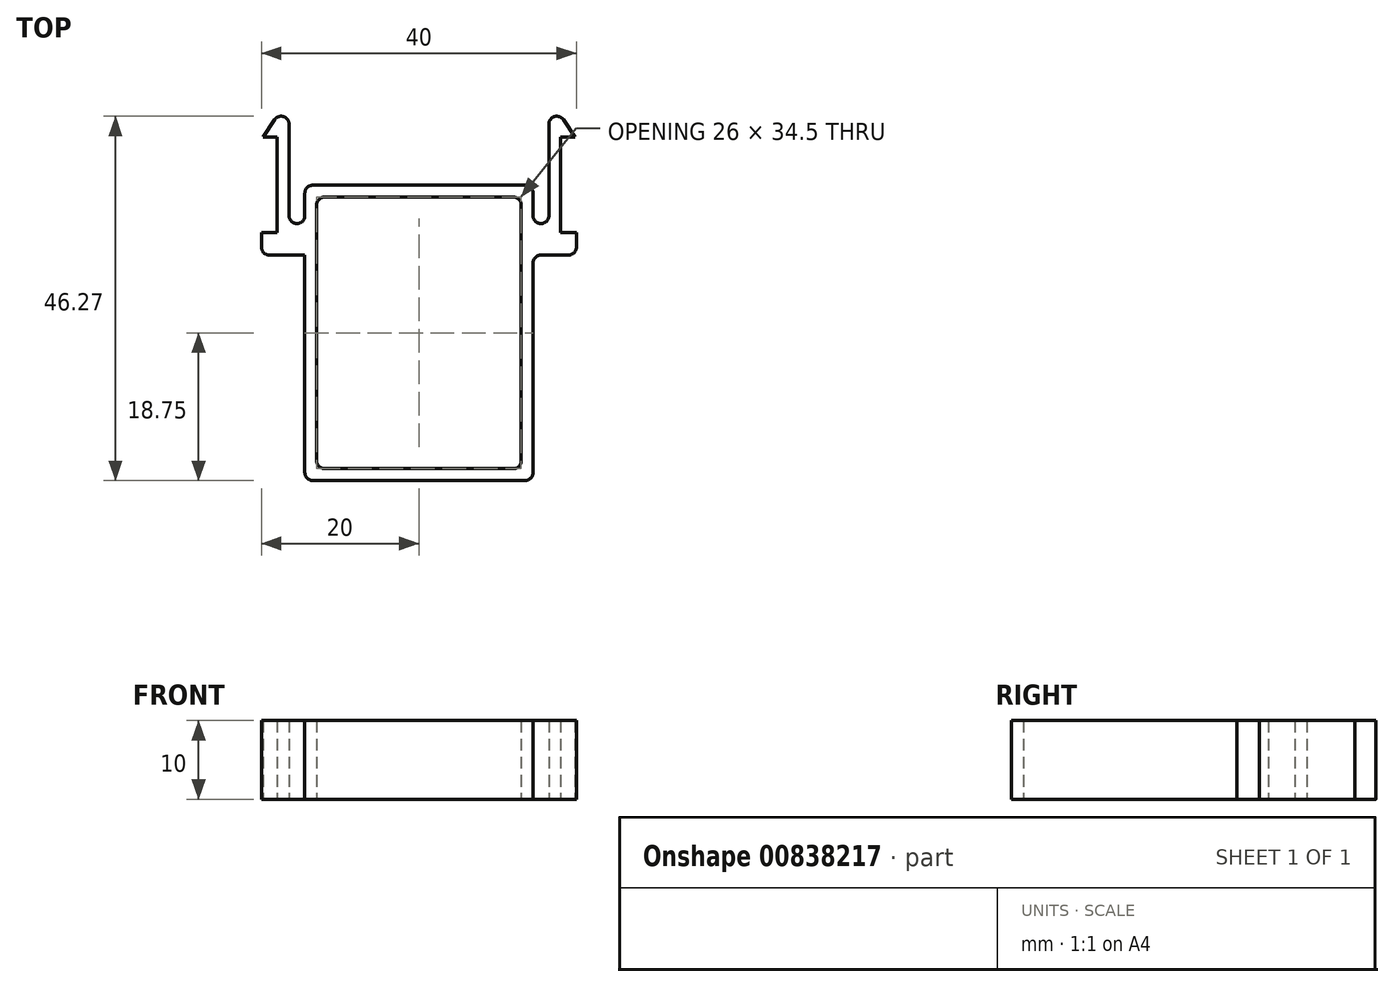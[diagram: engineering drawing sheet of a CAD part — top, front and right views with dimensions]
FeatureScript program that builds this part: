
annotation { "Feature Type Name" : "Feature", "Feature Type Description" : "" }
export const myFeature = defineFeature(function(context is Context, id is Id, definition is map)
    precondition{}
    {
        {
            var Q0;
            Q0=qCreatedBy(makeId("Top.planeOp"),FACE);
            var sketch = newSketch(context, id + "F0", { "sketchPlane" : qUnion([Q0])});
            skLineSegment(sketch, "E0.bottom", {"start": v(-13, 17.25) * mm, "end": v(13, 17.25) * mm});
            skLineSegment(sketch, "E0.top", {"start": v(-13, -17.25) * mm, "end": v(13, -17.25) * mm});
            skLineSegment(sketch, "E0.left", {"start": v(-13, 17.25) * mm, "end": v(-13, -17.25) * mm});
            skLineSegment(sketch, "E0.right", {"start": v(13, 17.25) * mm, "end": v(13, -17.25) * mm});
            skPoint(sketch, "E0.middle", {"position": v(0, 0) * mm});
            skLineSegment(sketch, "E1.0", {"start": v(-14.5, 18.75) * mm, "end": v(-14.5, -18.75) * mm});
            skLineSegment(sketch, "E1.1", {"start": v(-14.5, 18.75) * mm, "end": v(14.5, 18.75) * mm});
            skLineSegment(sketch, "E1.2", {"start": v(14.5, 18.75) * mm, "end": v(14.5, -18.75) * mm});
            skLineSegment(sketch, "E1.3", {"start": v(-14.5, -18.75) * mm, "end": v(14.5, -18.75) * mm});
            skLineSegment(sketch, "E2", {"start": v(0, -36.25) * mm, "end": v(0, 59.39) * mm, "construction": true});
            skLineSegment(sketch, "E3", {"start": v(-14.5, 9.88) * mm, "end": v(-16.5, 9.88) * mm});
            skLineSegment(sketch, "E4", {"start": v(-16.5, 9.88) * mm, "end": v(-16.5, 13.88) * mm});
            skLineSegment(sketch, "E5", {"start": v(-16.5, 13.88) * mm, "end": v(-14.5, 13.88) * mm});
            skLineSegment(sketch, "E6", {"start": v(-16.5, 9.88) * mm, "end": v(-16.5, 29.86) * mm});
            skLineSegment(sketch, "E7", {"start": v(-16.5, 29.86) * mm, "end": v(-19.8, 24.85) * mm});
            skLineSegment(sketch, "E8", {"start": v(-19.8, 24.85) * mm, "end": v(-18, 24.85) * mm});
            skLineSegment(sketch, "E9", {"start": v(-18, 24.85) * mm, "end": v(-18, 9.88) * mm});
            skLineSegment(sketch, "E10", {"start": v(-18, 9.88) * mm, "end": v(-16.5, 9.88) * mm});
            skLineSegment(sketch, "E11", {"start": v(-18, 9.88) * mm, "end": v(-20, 9.88) * mm});
            skLineSegment(sketch, "E12", {"start": v(-20, 9.88) * mm, "end": v(-20, 12.75) * mm});
            skLineSegment(sketch, "E13", {"start": v(-20, 12.75) * mm, "end": v(-18, 12.75) * mm});
            skLineSegment(sketch, "E14.MirrorCS", {"start": v(16.5, 9.88) * mm, "end": v(16.5, 29.86) * mm});
            skLineSegment(sketch, "E15.MirrorCS", {"start": v(16.5, 29.86) * mm, "end": v(19.8, 24.85) * mm});
            skLineSegment(sketch, "E16.MirrorCS", {"start": v(18, 24.85) * mm, "end": v(18, 9.88) * mm});
            skLineSegment(sketch, "E17.MirrorCS", {"start": v(20, 12.75) * mm, "end": v(18, 12.75) * mm});
            skLineSegment(sketch, "E18.MirrorCS", {"start": v(20, 9.88) * mm, "end": v(20, 12.75) * mm});
            skLineSegment(sketch, "E19.MirrorCS", {"start": v(18, 9.88) * mm, "end": v(20, 9.88) * mm});
            skLineSegment(sketch, "E20.MirrorCS", {"start": v(18, 9.88) * mm, "end": v(16.5, 9.88) * mm});
            skLineSegment(sketch, "E21.MirrorCS", {"start": v(14.5, 9.88) * mm, "end": v(16.5, 9.88) * mm});
            skLineSegment(sketch, "E22.MirrorCS", {"start": v(16.5, 13.88) * mm, "end": v(14.5, 13.88) * mm});
            skLineSegment(sketch, "E23.MirrorCS", {"start": v(19.8, 24.85) * mm, "end": v(18, 24.85) * mm});
            skLineSegment(sketch, "E24", {"start": v(-13, -2.29) * mm, "end": v(13, -2.29) * mm});
            skLineSegment(sketch, "E25", {"start": v(13, -2.29) * mm, "end": v(13, 4.71) * mm});
            skLineSegment(sketch, "E26", {"start": v(13, 4.71) * mm, "end": v(-13, 4.71) * mm});
            skSolve(sketch);
        }
        {
            var Q0;
            Q0=qSketchRegion(id+"F0",true);
            extrude(context, id + "F1", {"entities" : qUnion([Q0]), "depth" : 10 * mm, "offsetDistance" : 25 * mm});
        }
        {
            var Q0;
            Q0=makeQuery(id+"F1.opExtrude","SWEPT_EDGE",EDGE,{"disambiguationData":[OSD([sQuery(id+"F0.wireOp",EDGE,"E1.0"),sQuery(id+"F0.wireOp",EDGE,"E1.1")])]});
            var Q1;
            Q1=makeQuery(id+"F1.opExtrude","SWEPT_EDGE",EDGE,{"disambiguationData":[OSD([sQuery(id+"F0.wireOp",EDGE,"E11"),sQuery(id+"F0.wireOp",EDGE,"E12")])]});
            var Q2;
            Q2=makeQuery(id+"F1.opExtrude","SWEPT_EDGE",EDGE,{"disambiguationData":[OSD([sQuery(id+"F0.wireOp",EDGE,"E1.1"),sQuery(id+"F0.wireOp",EDGE,"E1.2")])]});
            var Q3;
            Q3=makeQuery(id+"F1.opExtrude","SWEPT_EDGE",EDGE,{"disambiguationData":[OSD([sQuery(id+"F0.wireOp",EDGE,"E18.MirrorCS"),sQuery(id+"F0.wireOp",EDGE,"E19.MirrorCS")])]});
            var Q4;
            Q4=makeQuery(id+"F1.opExtrude","SWEPT_EDGE",EDGE,{"disambiguationData":[OSD([sQuery(id+"F0.wireOp",EDGE,"E0.bottom"),sQuery(id+"F0.wireOp",EDGE,"E0.left")])]});
            var Q5;
            Q5=makeQuery(id+"F1.opExtrude","SWEPT_EDGE",EDGE,{"disambiguationData":[OSD([sQuery(id+"F0.wireOp",EDGE,"E1.2"),sQuery(id+"F0.wireOp",EDGE,"E21.MirrorCS")])]});
            var Q6;
            Q6=makeQuery(id+"F1.opExtrude","SWEPT_EDGE",EDGE,{"disambiguationData":[OSD([sQuery(id+"F0.wireOp",EDGE,"E1.2"),sQuery(id+"F0.wireOp",EDGE,"E1.3")])]});
            var Q7;
            Q7=makeQuery(id+"F1.opExtrude","SWEPT_EDGE",EDGE,{"disambiguationData":[OSD([sQuery(id+"F0.wireOp",EDGE,"E1.0"),sQuery(id+"F0.wireOp",EDGE,"E1.3")])]});
            var Q8;
            Q8=makeQuery(id+"F1.opExtrude","SWEPT_EDGE",EDGE,{"disambiguationData":[OSD([sQuery(id+"F0.wireOp",EDGE,"E0.top"),sQuery(id+"F0.wireOp",EDGE,"E0.left")])]});
            var Q9;
            Q9=makeQuery(id+"F1.opExtrude","SWEPT_EDGE",EDGE,{"disambiguationData":[OSD([sQuery(id+"F0.wireOp",EDGE,"E0.bottom"),sQuery(id+"F0.wireOp",EDGE,"E0.right")])]});
            var Q10;
            Q10=makeQuery(id+"F1.opExtrude","SWEPT_EDGE",EDGE,{"disambiguationData":[OSD([sQuery(id+"F0.wireOp",EDGE,"E0.top"),sQuery(id+"F0.wireOp",EDGE,"E0.right")])]});
            var Q11;
            Q11=makeQuery(id+"F1.opExtrude","SWEPT_EDGE",EDGE,{"disambiguationData":[OSD([sQuery(id+"F0.wireOp",EDGE,"E1.0"),sQuery(id+"F0.wireOp",EDGE,"E5")])]});
            var Q12;
            Q12=makeQuery(id+"F1.opExtrude","SWEPT_EDGE",EDGE,{"disambiguationData":[OSD([sQuery(id+"F0.wireOp",EDGE,"E14.MirrorCS"),sQuery(id+"F0.wireOp",EDGE,"E22.MirrorCS")])]});
            var Q13;
            Q13=makeQuery(id+"F1.opExtrude","SWEPT_EDGE",EDGE,{"disambiguationData":[OSD([sQuery(id+"F0.wireOp",EDGE,"E5"),sQuery(id+"F0.wireOp",EDGE,"E6")])]});
            var Q14;
            Q14=makeQuery(id+"F1.opExtrude","SWEPT_EDGE",EDGE,{"disambiguationData":[OSD([sQuery(id+"F0.wireOp",EDGE,"E1.2"),sQuery(id+"F0.wireOp",EDGE,"E22.MirrorCS")])]});
            var Q15;
            Q15=makeQuery(id+"F1.opExtrude","SWEPT_EDGE",EDGE,{"disambiguationData":[OSD([sQuery(id+"F0.wireOp",EDGE,"E6"),sQuery(id+"F0.wireOp",EDGE,"E7")])]});
            var Q16;
            Q16=makeQuery(id+"F1.opExtrude","SWEPT_EDGE",EDGE,{"disambiguationData":[OSD([sQuery(id+"F0.wireOp",EDGE,"E14.MirrorCS"),sQuery(id+"F0.wireOp",EDGE,"E15.MirrorCS")])]});
            fillet(context, id + "F2", {"entities" : qUnion([Q0, Q1, Q2, Q3, Q4, Q5, Q6, Q7, Q8, Q9, Q10, Q11, Q12, Q13, Q14, Q15, Q16]), "radius" : 1 * mm, "tangentPropagation" : true, "allowEdgeOverflow" : false});
        }
    });
